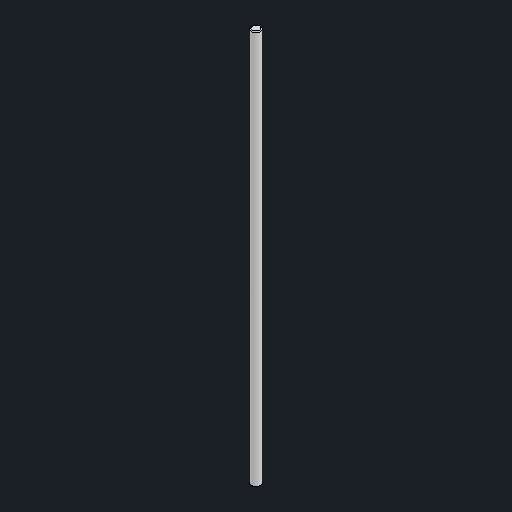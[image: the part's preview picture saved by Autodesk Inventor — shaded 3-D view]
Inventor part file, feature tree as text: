
AUTODESK INVENTOR PART (.ipt)
format: ipt  version: 2024.2 (Build 282272000, 272)  size: 68,096 bytes
history: native  units: mm
features: other x1, chamfer x1
ambient origin geometry x8: Origin, YZ Plane, XZ Plane, XY Plane, X Axis, Y Axis, Z Axis, Center Point
bodies: Body1 (feature_tree)
feature tree (2):
  other  "솔리드1"
  chamfer  "Chamfer1"  [1 undecoded]
note: 1 required parameter value undecoded (feature->parameter linkage not recoverable at this tier; creation-order binding heuristic only, values carry confidence <= 0.55)
